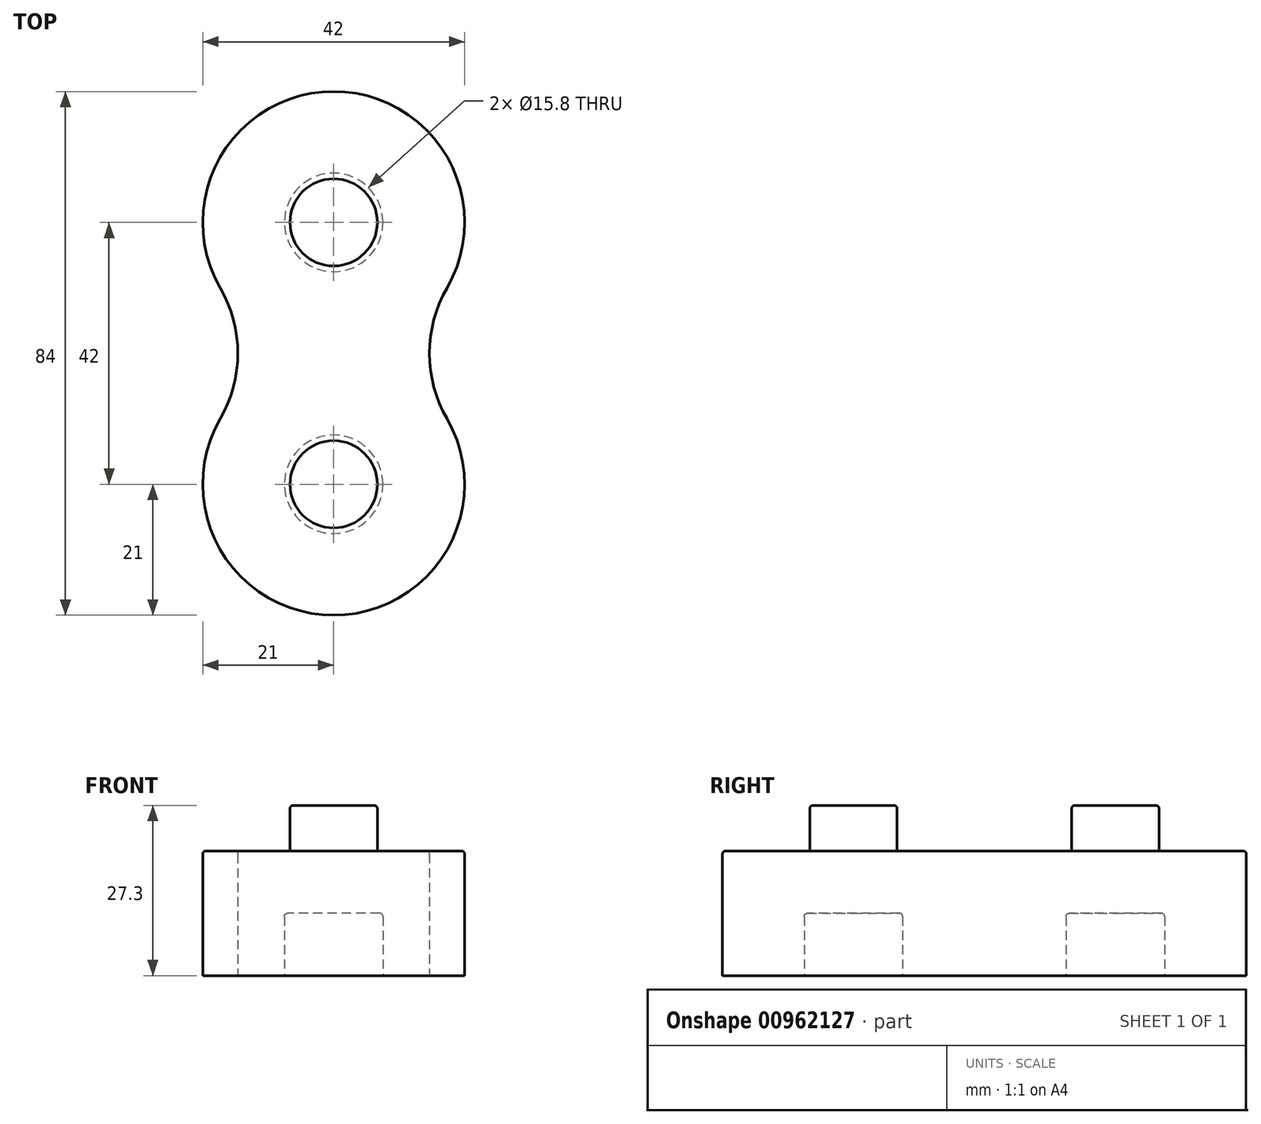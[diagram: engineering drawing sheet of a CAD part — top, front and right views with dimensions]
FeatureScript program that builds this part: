
annotation { "Feature Type Name" : "Feature", "Feature Type Description" : "" }
export const myFeature = defineFeature(function(context is Context, id is Id, definition is map)
    precondition{}
    {
        {
            assignVariable(context, id + "F0", {"name" : "inner_circle_extrude", "anyValue" : 10});
        }
        {
            assignVariable(context, id + "F1", {"name" : "nipple_circle_extrude", "anyValue" : 7.3});
        }
        {
            assignVariable(context, id + "F2", {"name" : "outer_circle_extrude", "anyValue" : 20});
        }
        {
            assignVariable(context, id + "F3", {"name" : "fillet", "anyValue" : 0.5});
        }
        {
            var Q0;
            Q0=qCreatedBy(makeId("Top.planeOp"),FACE);
            var sketch = newSketch(context, id + "F4", { "sketchPlane" : qUnion([Q0])});
            skCircle(sketch, "E0", {"center": v(0, 42) * mm, "radius": 7.9 * mm});
            skCircle(sketch, "E1", {"center": v(0, 0) * mm, "radius": 7.9 * mm});
            skArc(sketch, "E2.converted", {"start": v(18.19, 31.5) * mm, "mid": v(0, 63) * mm, "end": v(-18.19, 31.5) * mm});
            skArc(sketch, "E3.converted", {"start": v(-18.19, 10.5) * mm, "mid": v(0, -21) * mm, "end": v(18.19, 10.5) * mm});
            skPoint(sketch, "E4.orphan", {"position": v(-18.87, 9.22) * mm});
            skArc(sketch, "E5", {"start": v(-18.19, 10.5) * mm, "mid": v(-15.37, 21) * mm, "end": v(-18.19, 31.5) * mm});
            skArc(sketch, "E6.MirrorC", {"start": v(18.19, 10.5) * mm, "mid": v(15.37, 21) * mm, "end": v(18.19, 31.5) * mm});
            skSolve(sketch);
        }
        {
            var Q0;
            Q0=makeQuery(id+"F4.imprint","IMPRINT",FACE,{"disambiguationData":[TD([[makeQuery(id+"F4.imprint","IMPRINT",EDGE,{"derivedFrom":sQuery(id+"F4.wireOp",EDGE,"ScaTM9CG-l0WX-AUfX-dH3G-diZ5i2Zft3Bz")}),1.0]])]});
            var Q1;
            Q1=makeQuery(id+"F4.imprint","IMPRINT",FACE,{"disambiguationData":[TD([[makeQuery(id+"F4.imprint","IMPRINT",EDGE,{"derivedFrom":sQuery(id+"F4.wireOp",EDGE,"E0")}),1.0]])]});
            var Q2;
            Q2=makeQuery(id+"F4.imprint","IMPRINT",FACE,{"disambiguationData":[TD([[makeQuery(id+"F4.imprint","IMPRINT",EDGE,{"derivedFrom":sQuery(id+"F4.wireOp",EDGE,"E1")}),1.0]])]});
            var Q3;
            Q3=makeQuery(id+"F4.imprint","IMPRINT",FACE,{"disambiguationData":[TD([[makeQuery(id+"F4.imprint","IMPRINT",EDGE,{"derivedFrom":sQuery(id+"F4.wireOp",EDGE,"E0")}),-1.0]])]});
            extrude(context, id + "F5", {"entities" : qUnion([Q0, Q1, Q2, Q3]), "depth" : (getVariable(context, 'outer_circle_extrude')) * mm, "offsetDistance" : 25 * mm});
        }
        {
            var Q0;
            Q0=makeQuery(id+"F4.imprint","IMPRINT",FACE,{"disambiguationData":[TD([[makeQuery(id+"F4.imprint","IMPRINT",EDGE,{"derivedFrom":sQuery(id+"F4.wireOp",EDGE,"E0")}),1.0]])]});
            var Q1;
            Q1=makeQuery(id+"F4.imprint","IMPRINT",FACE,{"disambiguationData":[TD([[makeQuery(id+"F4.imprint","IMPRINT",EDGE,{"derivedFrom":sQuery(id+"F4.wireOp",EDGE,"E1")}),1.0]])]});
            extrude(context, id + "F6", {"entities" : qUnion([Q0, Q1]), "operationType" : NewBodyOperationType.REMOVE, "depth" : (getVariable(context, 'inner_circle_extrude')) * mm, "offsetDistance" : 25 * mm});
        }
        {
            var Q0;
            Q0=makeQuery(id+"F5.opExtrude","CAP_FACE",FACE,{"disambiguationData":[OSD([sQuery(id+"F4.wireOp",EDGE,"E2.converted"),sQuery(id+"F4.wireOp",EDGE,"E3.converted"),sQuery(id+"F4.wireOp",EDGE,"E5"),sQuery(id+"F4.wireOp",EDGE,"E6.MirrorC")])],"isStart":false});
            var sketch = newSketch(context, id + "F7", { "sketchPlane" : qUnion([Q0])});
            skCircle(sketch, "E7", {"center": v(0, 0) * mm, "radius": 7 * mm});
            skCircle(sketch, "E8", {"center": v(0, 42) * mm, "radius": 7 * mm});
            skSolve(sketch);
        }
        {
            var Q0;
            Q0=makeQuery(id+"F7.imprint","IMPRINT",FACE,{"disambiguationData":[TD([[makeQuery(id+"F7.imprint","IMPRINT",EDGE,{"derivedFrom":sQuery(id+"F7.wireOp",EDGE,"E7")}),1.0]])]});
            var Q1;
            Q1=makeQuery(id+"F7.imprint","IMPRINT",FACE,{"disambiguationData":[TD([[makeQuery(id+"F7.imprint","IMPRINT",EDGE,{"derivedFrom":sQuery(id+"F7.wireOp",EDGE,"Dg55u7MG-Wcnn-qXMQ-j3jR-78wnB7IFwmOc")}),1.0]])]});
            var Q2;
            Q2=makeQuery(id+"F7.imprint","IMPRINT",FACE,{"disambiguationData":[TD([[makeQuery(id+"F7.imprint","IMPRINT",EDGE,{"derivedFrom":sQuery(id+"F7.wireOp",EDGE,"E8")}),1.0]])]});
            extrude(context, id + "F8", {"entities" : qUnion([Q0, Q1, Q2]), "operationType" : NewBodyOperationType.ADD, "depth" : (getVariable(context, 'nipple_circle_extrude')) * mm, "offsetDistance" : 25 * mm});
        }
        {
            var Q0;
            Q0=makeQuery(id+"F8.opExtrude","CAP_EDGE",EDGE,{"disambiguationData":[OSD([sQuery(id+"F7.wireOp",EDGE,"E7")])],"isStart":false});
            var Q1;
            Q1=makeQuery(id+"F5.opExtrude","CAP_EDGE",EDGE,{"disambiguationData":[OSD([sQuery(id+"F4.wireOp",EDGE,"ScaTM9CG-l0WX-AUfX-dH3G-diZ5i2Zft3Bz")])],"isStart":false});
            var Q2;
            Q2=makeQuery(id+"F5.opExtrude","CAP_EDGE",EDGE,{"disambiguationData":[OSD([sQuery(id+"F4.wireOp",EDGE,"ScaTM9CG-l0WX-AUfX-dH3G-diZ5i2Zft3Bz")])],"isStart":true});
            var Q3;
            Q3=makeQuery(id+"F6.boolean.opBoolean","COPY",EDGE,{"derivedFrom":makeQuery(id+"F6.opExtrude","CAP_EDGE",EDGE,{"disambiguationData":[OSD([sQuery(id+"F4.wireOp",EDGE,"E0")])],"isStart":true})});
            var Q4;
            Q4=makeQuery(id+"F6.boolean.opBoolean","COPY",FACE,{"derivedFrom":makeQuery(id+"F6.opExtrude","CAP_FACE",FACE,{"disambiguationData":[OSD([sQuery(id+"F4.wireOp",EDGE,"E0")])],"isStart":false})});
            var Q5;
            Q5=makeQuery(id+"F6.boolean.opBoolean","COPY",EDGE,{"derivedFrom":makeQuery(id+"F6.opExtrude","CAP_EDGE",EDGE,{"disambiguationData":[OSD([sQuery(id+"F4.wireOp",EDGE,"E1")])],"isStart":true})});
            var Q6;
            Q6=makeQuery(id+"F6.boolean.opBoolean","COPY",EDGE,{"derivedFrom":makeQuery(id+"F6.opExtrude","CAP_EDGE",EDGE,{"disambiguationData":[OSD([sQuery(id+"F4.wireOp",EDGE,"E1")])],"isStart":false})});
            var Q7;
            Q7=makeQuery(id+"F8.opExtrude","CAP_EDGE",EDGE,{"disambiguationData":[OSD([sQuery(id+"F7.wireOp",EDGE,"Dg55u7MG-Wcnn-qXMQ-j3jR-78wnB7IFwmOc")])],"isStart":true});
            var Q8;
            Q8=makeQuery(id+"F8.opExtrude","CAP_EDGE",EDGE,{"disambiguationData":[OSD([sQuery(id+"F7.wireOp",EDGE,"Dg55u7MG-Wcnn-qXMQ-j3jR-78wnB7IFwmOc")])],"isStart":false});
            var Q9;
            Q9=makeQuery(id+"F8.opExtrude","CAP_EDGE",EDGE,{"disambiguationData":[OSD([sQuery(id+"F7.wireOp",EDGE,"E8")])],"isStart":false});
            var Q10;
            Q10=makeQuery(id+"F8.opExtrude","CAP_EDGE",EDGE,{"disambiguationData":[OSD([sQuery(id+"F7.wireOp",EDGE,"E8")])],"isStart":true});
            var Q11;
            Q11=makeQuery(id+"F5.opExtrude","CAP_EDGE",EDGE,{"disambiguationData":[OSD([sQuery(id+"F4.wireOp",EDGE,"E2.converted")])],"isStart":false});
            var Q12;
            Q12=makeQuery(id+"F8.opExtrude","CAP_EDGE",EDGE,{"disambiguationData":[OSD([sQuery(id+"F7.wireOp",EDGE,"E7")])],"isStart":true});
            fillet(context, id + "F9", {"entities" : qUnion([Q0, Q1, Q2, Q3, Q4, Q5, Q6, Q7, Q8, Q9, Q10, Q11, Q12]), "radius" : (getVariable(context, 'fillet')) * mm, "tangentPropagation" : true, "allowEdgeOverflow" : false});
        }
    });
